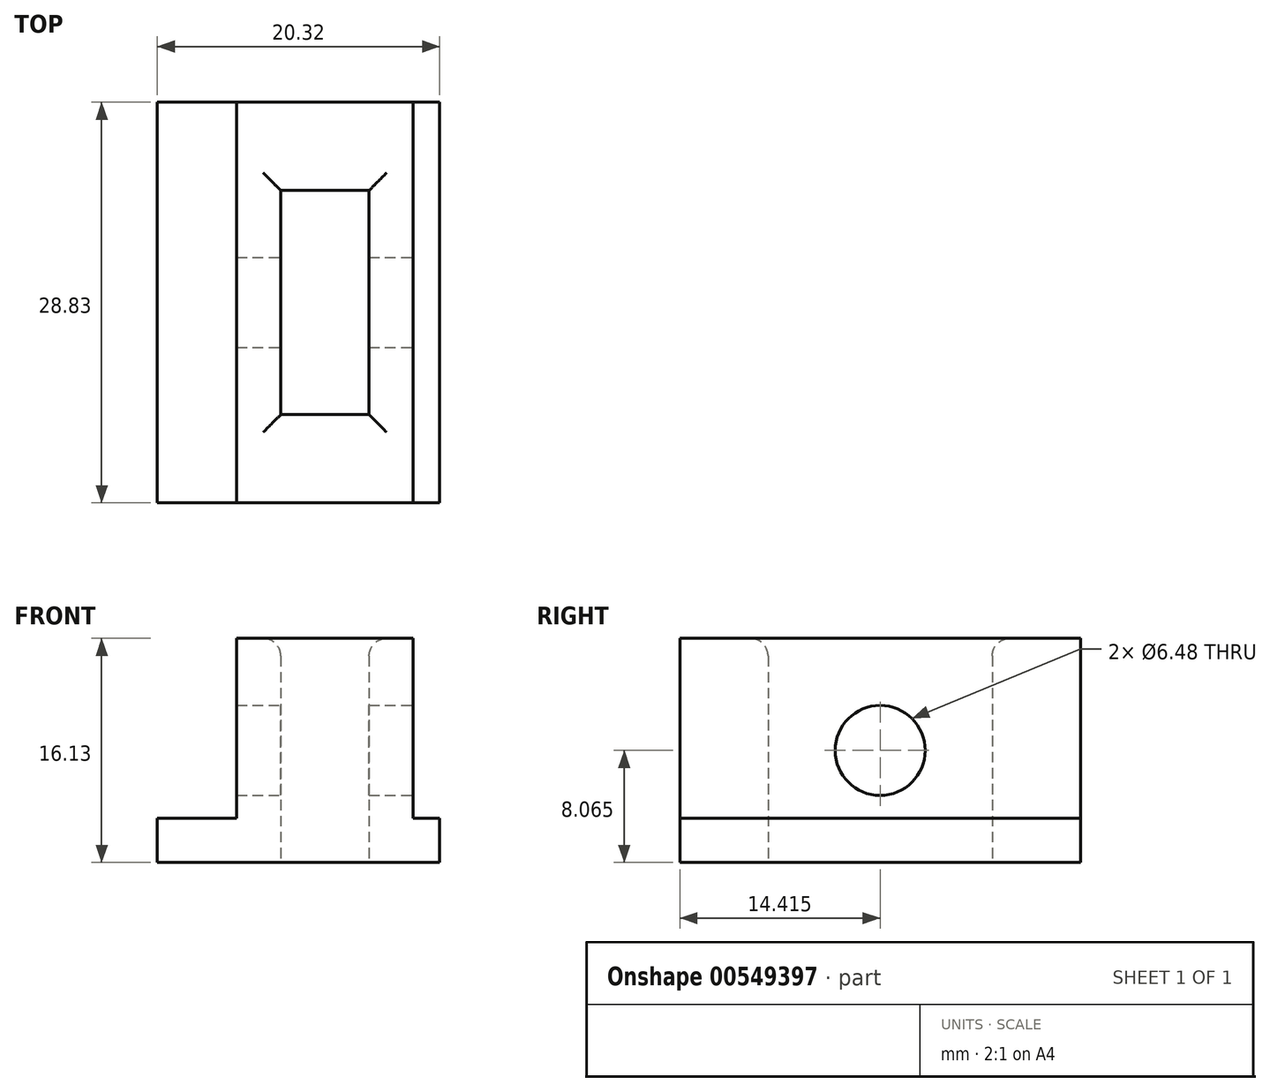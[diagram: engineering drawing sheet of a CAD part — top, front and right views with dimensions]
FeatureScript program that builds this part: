
annotation { "Feature Type Name" : "Feature", "Feature Type Description" : "" }
export const myFeature = defineFeature(function(context is Context, id is Id, definition is map)
    precondition{}
    {
        {
            var Q0;
            Q0=qCreatedBy(makeId("Top.planeOp"),FACE);
            var sketch = newSketch(context, id + "F0", { "sketchPlane" : qUnion([Q0])});
            skLineSegment(sketch, "E0.bottom", {"start": v(-3.18, 16.13) * mm, "end": v(3.18, 16.13) * mm});
            skLineSegment(sketch, "E0.top", {"start": v(-3.18, 0) * mm, "end": v(3.18, 0) * mm});
            skLineSegment(sketch, "E0.left", {"start": v(-3.18, 16.13) * mm, "end": v(-3.18, 0) * mm});
            skLineSegment(sketch, "E0.right", {"start": v(3.18, 16.13) * mm, "end": v(3.18, 0) * mm});
            skLineSegment(sketch, "E1.bottom", {"start": v(8.26, -6.35) * mm, "end": v(-12.06, -6.35) * mm});
            skLineSegment(sketch, "E1.top", {"start": v(8.25, 22.48) * mm, "end": v(-12.07, 22.48) * mm});
            skLineSegment(sketch, "E1.left", {"start": v(8.26, -6.35) * mm, "end": v(8.25, 22.48) * mm});
            skLineSegment(sketch, "E1.right", {"start": v(-12.07, -6.35) * mm, "end": v(-12.07, 22.48) * mm});
            skLineSegment(sketch, "E2.bottom", {"start": v(-6.35, 22.48) * mm, "end": v(6.35, 22.48) * mm});
            skLineSegment(sketch, "E2.top", {"start": v(-6.35, -6.35) * mm, "end": v(6.35, -6.35) * mm});
            skLineSegment(sketch, "E2.left", {"start": v(-6.35, 22.48) * mm, "end": v(-6.35, -6.35) * mm});
            skLineSegment(sketch, "E2.right", {"start": v(6.35, 22.48) * mm, "end": v(6.35, -6.35) * mm});
            skSolve(sketch);
        }
        {
            var Q0;
            Q0=makeQuery(id+"F0.imprint","IMPRINT",FACE,{"disambiguationData":[TD([[makeQuery(id+"F0.imprint","IMPRINT",EDGE,{"derivedFrom":sQuery(id+"F0.wireOp",EDGE,"E0.bottom")}),1.0]])]});
            var Q1;
            {var subQ0=sQuery(id+"F0.wireOp",EDGE,"E1.right");Q1=makeQuery(id+"F0.imprint","IMPRINT",FACE,{"disambiguationData":[TD([[makeQuery(id+"F0.imprint","IMPRINT",EDGE,{"derivedFrom":subQ0}),-1.0]])]});}
            var Q2;
            {var subQ0=sQuery(id+"F0.wireOp",EDGE,"E1.left");Q2=makeQuery(id+"F0.imprint","IMPRINT",FACE,{"disambiguationData":[TD([[makeQuery(id+"F0.imprint","IMPRINT",EDGE,{"derivedFrom":subQ0}),1.0]])]});}
            extrude(context, id + "F1", {"entities" : qUnion([Q0, Q1, Q2]), "depth" : 3.17 * mm, "offsetDistance" : 25.4 * mm});
        }
        {
            var Q0;
            Q0=makeQuery(id+"F0.imprint","IMPRINT",FACE,{"disambiguationData":[TD([[makeQuery(id+"F0.imprint","IMPRINT",EDGE,{"derivedFrom":sQuery(id+"F0.wireOp",EDGE,"E0.bottom")}),1.0]])]});
            extrude(context, id + "F2", {"entities" : qUnion([Q0]), "operationType" : NewBodyOperationType.ADD, "depth" : 16.13 * mm, "offsetDistance" : 25.4 * mm});
        }
        {
            var Q0;
            Q0=makeQuery(id+"F2.opExtrude","SWEPT_FACE",FACE,{"disambiguationData":[OSD([sQuery(id+"F0.wireOp",EDGE,"E2.right")])]});
            var sketch = newSketch(context, id + "F3", { "sketchPlane" : qUnion([Q0])});
            skLineSegment(sketch, "E3", {"start": v(0, 0) * mm, "end": v(0, 17.91) * mm, "construction": true});
            skLineSegment(sketch, "E4", {"start": v(16.13, 0) * mm, "end": v(16.13, 17.9) * mm, "construction": true});
            skCircle(sketch, "E5", {"center": v(8.06, 8.06) * mm, "radius": 3.24 * mm});
            skSolve(sketch);
        }
        {
            var Q0;
            Q0=makeQuery(id+"F3.imprint","IMPRINT",FACE,{"disambiguationData":[TD([[makeQuery(id+"F3.imprint","IMPRINT",EDGE,{"derivedFrom":sQuery(id+"F3.wireOp",EDGE,"E5")}),1.0]])]});
            extrude(context, id + "F4", {"entities" : qUnion([Q0]), "operationType" : NewBodyOperationType.REMOVE, "endBound" : BoundingType.THROUGH_ALL, "oppositeDirection" : true, "depth" : 25.4 * mm, "offsetDistance" : 25.4 * mm});
        }
        {
            var Q0;
            Q0=makeQuery(id+"F2.opExtrude","CAP_EDGE",EDGE,{"disambiguationData":[OSD([sQuery(id+"F0.wireOp",EDGE,"E0.right")])],"isStart":false});
            var Q1;
            Q1=makeQuery(id+"F2.opExtrude","CAP_EDGE",EDGE,{"disambiguationData":[OSD([sQuery(id+"F0.wireOp",EDGE,"E0.left")])],"isStart":false});
            var Q2;
            Q2=makeQuery(id+"F2.opExtrude","CAP_EDGE",EDGE,{"disambiguationData":[OSD([sQuery(id+"F0.wireOp",EDGE,"E0.top")])],"isStart":false});
            var Q3;
            Q3=makeQuery(id+"F2.opExtrude","CAP_EDGE",EDGE,{"disambiguationData":[OSD([sQuery(id+"F0.wireOp",EDGE,"E0.bottom")])],"isStart":false});
            fillet(context, id + "F5", {"entities" : qUnion([Q0, Q1, Q2, Q3]), "radius" : 1.27 * mm, "tangentPropagation" : true, "allowEdgeOverflow" : false});
        }
    });
